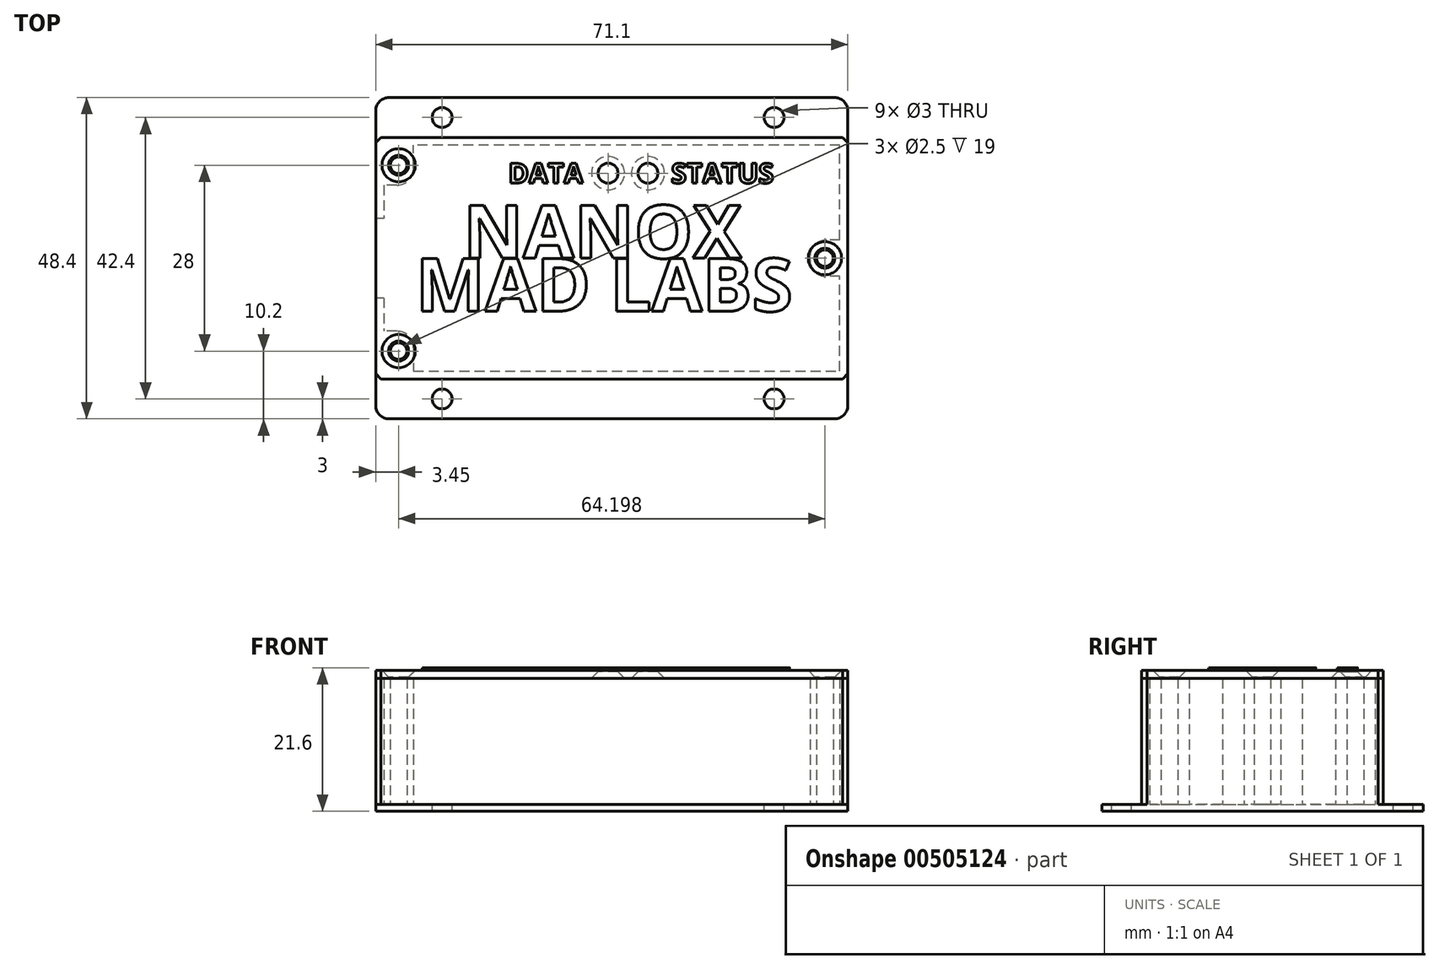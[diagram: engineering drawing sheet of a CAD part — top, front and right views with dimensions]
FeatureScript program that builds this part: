
annotation { "Feature Type Name" : "Feature", "Feature Type Description" : "" }
export const myFeature = defineFeature(function(context is Context, id is Id, definition is map)
    precondition{}
    {
        {
            var Q0;
            Q0=qCreatedBy(makeId("Top.planeOp"),FACE);
            var sketch = newSketch(context, id + "F0", { "sketchPlane" : qUnion([Q0])});
            skLineSegment(sketch, "E0", {"start": v(0, 6) * mm, "end": v(71.1, 6) * mm});
            skLineSegment(sketch, "E1", {"start": v(71.1, 6) * mm, "end": v(71.1, 42.4) * mm});
            skLineSegment(sketch, "E2", {"start": v(71.1, 42.4) * mm, "end": v(0, 42.4) * mm});
            skLineSegment(sketch, "E3", {"start": v(1.2, 18.2) * mm, "end": v(0, 18.2) * mm});
            skLineSegment(sketch, "E4", {"start": v(0, 18.2) * mm, "end": v(0, 6) * mm});
            skLineSegment(sketch, "E5", {"start": v(1.2, 30.2) * mm, "end": v(0, 30.2) * mm});
            skLineSegment(sketch, "E6", {"start": v(0, 30.2) * mm, "end": v(0, 42.4) * mm});
            skLineSegment(sketch, "E7", {"start": v(0, 6) * mm, "end": v(0, 0) * mm});
            skLineSegment(sketch, "E8", {"start": v(0, 0) * mm, "end": v(71.1, 0) * mm});
            skLineSegment(sketch, "E9", {"start": v(71.1, 48.4) * mm, "end": v(0, 48.4) * mm});
            skLineSegment(sketch, "E10", {"start": v(0, 42.4) * mm, "end": v(0, 48.4) * mm});
            skLineSegment(sketch, "E11", {"start": v(71.1, 0) * mm, "end": v(71.1, 6) * mm});
            skLineSegment(sketch, "E12", {"start": v(71.1, 42.4) * mm, "end": v(71.1, 48.4) * mm});
            skCircle(sketch, "E13", {"center": v(10, 3) * mm, "radius": 1.5 * mm});
            skCircle(sketch, "E14", {"center": v(60, 3) * mm, "radius": 1.5 * mm});
            skCircle(sketch, "E15", {"center": v(10, 45.4) * mm, "radius": 1.5 * mm});
            skLineSegment(sketch, "E16", {"start": v(60, 45.4) * mm, "end": v(60, 3) * mm, "construction": true});
            skLineSegment(sketch, "E17", {"start": v(10, 45.4) * mm, "end": v(10, 3) * mm, "construction": true});
            skCircle(sketch, "E18", {"center": v(60, 45.4) * mm, "radius": 1.5 * mm});
            skLineSegment(sketch, "E19", {"start": v(10, 45.4) * mm, "end": v(60, 45.4) * mm, "construction": true});
            skLineSegment(sketch, "E20", {"start": v(60, 3) * mm, "end": v(10, 3) * mm, "construction": true});
            skLineSegment(sketch, "E21", {"start": v(0, 18.2) * mm, "end": v(0, 30.2) * mm});
            skLineSegment(sketch, "E22", {"start": v(3.45, 10.2) * mm, "end": v(3.45, 38.2) * mm, "construction": true});
            skCircle(sketch, "E23", {"center": v(3.45, 38.2) * mm, "radius": 1.25 * mm});
            skCircle(sketch, "E24", {"center": v(3.45, 10.2) * mm, "radius": 1.25 * mm});
            skLineSegment(sketch, "E25.bottom", {"start": v(5.7, 13.2) * mm, "end": v(1.2, 13.2) * mm});
            skLineSegment(sketch, "E25.left", {"start": v(5.7, 13.2) * mm, "end": v(5.7, 7.2) * mm});
            skLineSegment(sketch, "E26.bottom", {"start": v(5.7, 35.2) * mm, "end": v(1.2, 35.2) * mm});
            skLineSegment(sketch, "E26.left", {"start": v(5.7, 35.2) * mm, "end": v(5.7, 41.2) * mm});
            skLineSegment(sketch, "E27.bottom", {"start": v(69.9, 21.45) * mm, "end": v(65.4, 21.45) * mm});
            skLineSegment(sketch, "E27.top", {"start": v(69.9, 26.95) * mm, "end": v(65.4, 26.95) * mm});
            skLineSegment(sketch, "E27.right", {"start": v(65.4, 21.45) * mm, "end": v(65.4, 26.95) * mm});
            skCircle(sketch, "E28", {"center": v(67.65, 24.2) * mm, "radius": 1.25 * mm});
            skLineSegment(sketch, "E29", {"start": v(5.7, 7.2) * mm, "end": v(69.9, 7.2) * mm});
            skLineSegment(sketch, "E30", {"start": v(1.2, 35.2) * mm, "end": v(1.2, 30.2) * mm});
            skLineSegment(sketch, "E31", {"start": v(1.2, 18.2) * mm, "end": v(1.2, 13.2) * mm});
            skLineSegment(sketch, "E32", {"start": v(69.9, 41.2) * mm, "end": v(5.7, 41.2) * mm});
            skLineSegment(sketch, "E33", {"start": v(69.9, 7.2) * mm, "end": v(69.9, 21.45) * mm});
            skLineSegment(sketch, "E34", {"start": v(69.9, 26.95) * mm, "end": v(69.9, 41.2) * mm});
            skSolve(sketch);
        }
        {
            var Q0;
            Q0=makeQuery(id+"F0.imprint","IMPRINT",FACE,{"disambiguationData":[TD([[makeQuery(id+"F0.imprint","IMPRINT",EDGE,{"derivedFrom":sQuery(id+"F0.wireOp",EDGE,"9c3Mvh7g-mxJt-K1xE-6H6P-Ljy5htNZZuxI")}),1.0]])]});
            var Q1;
            Q1=makeQuery(id+"F0.imprint","IMPRINT",FACE,{"disambiguationData":[TD([[makeQuery(id+"F0.imprint","IMPRINT",EDGE,{"derivedFrom":sQuery(id+"F0.wireOp",EDGE,"E0")}),1.0]])]});
            extrude(context, id + "F1", {"entities" : qUnion([Q0, Q1]), "depth" : 19 * mm});
        }
        {
            var Q0;
            Q0 = qSketchRegion(id + "F0", true);
            var Q1;
            Q1=makeQuery(id+"F0.imprint","IMPRINT",FACE,{"disambiguationData":[TD([[makeQuery(id+"F0.imprint","IMPRINT",EDGE,{"derivedFrom":sQuery(id+"F0.wireOp",EDGE,"E27.bottom")}),-1.0]])]});
            var Q2;
            Q2=makeQuery(id+"F0.imprint","IMPRINT",FACE,{"disambiguationData":[TD([[makeQuery(id+"F0.imprint","IMPRINT",EDGE,{"derivedFrom":sQuery(id+"F0.wireOp",EDGE,"E24")}),-1.0]])]});
            var Q3;
            Q3=makeQuery(id+"F0.imprint","IMPRINT",FACE,{"disambiguationData":[TD([[makeQuery(id+"F0.imprint","IMPRINT",EDGE,{"derivedFrom":sQuery(id+"F0.wireOp",EDGE,"E23")}),-1.0]])]});
            var Q4;
            Q4=makeQuery(id+"F0.imprint","IMPRINT",FACE,{"disambiguationData":[TD([[makeQuery(id+"F0.imprint","IMPRINT",EDGE,{"derivedFrom":sQuery(id+"F0.wireOp",EDGE,"E24")}),1.0]])]});
            var Q5;
            Q5=makeQuery(id+"F0.imprint","IMPRINT",FACE,{"disambiguationData":[TD([[makeQuery(id+"F0.imprint","IMPRINT",EDGE,{"derivedFrom":sQuery(id+"F0.wireOp",EDGE,"E28")}),1.0]])]});
            var Q6;
            Q6=makeQuery(id+"F0.imprint","IMPRINT",FACE,{"disambiguationData":[TD([[makeQuery(id+"F0.imprint","IMPRINT",EDGE,{"derivedFrom":sQuery(id+"F0.wireOp",EDGE,"E23")}),1.0]])]});
            extrude(context, id + "F2", {"entities" : qUnion([Q0, Q1, Q2, Q3, Q4, Q5, Q6]), "operationType" : NewBodyOperationType.ADD, "depth" : -1 * mm});
        }
        {
            var Q0;
            Q0=makeQuery(id+"F2.opExtrude","SWEPT_EDGE",EDGE,{"disambiguationData":[OSD([sQuery(id+"F0.wireOp",EDGE,"E7"),sQuery(id+"F0.wireOp",EDGE,"E8")])]});
            var Q1;
            Q1=makeQuery(id+"F2.opExtrude","SWEPT_EDGE",EDGE,{"disambiguationData":[OSD([sQuery(id+"F0.wireOp",EDGE,"E8"),sQuery(id+"F0.wireOp",EDGE,"E11")])]});
            var Q2;
            Q2=makeQuery(id+"F2.opExtrude","SWEPT_EDGE",EDGE,{"disambiguationData":[OSD([sQuery(id+"F0.wireOp",EDGE,"E9"),sQuery(id+"F0.wireOp",EDGE,"E12")])]});
            var Q3;
            Q3=makeQuery(id+"F2.opExtrude","SWEPT_EDGE",EDGE,{"disambiguationData":[OSD([sQuery(id+"F0.wireOp",EDGE,"E9"),sQuery(id+"F0.wireOp",EDGE,"E10")])]});
            fillet(context, id + "F3", {"entities" : qUnion([Q0, Q1, Q2, Q3]), "radius" : 2 * mm, "tangentPropagation" : true, "allowEdgeOverflow" : false});
        }
        {
            var Q0;
            Q0=makeQuery(id+"F1.opExtrude","SWEPT_EDGE",EDGE,{"disambiguationData":[OSD([sQuery(id+"F0.wireOp",EDGE,"E2"),sQuery(id+"F0.wireOp",EDGE,"E6"),sQuery(id+"F0.wireOp",EDGE,"E10")])]});
            var Q1;
            Q1=makeQuery(id+"F1.opExtrude","SWEPT_EDGE",EDGE,{"disambiguationData":[OSD([sQuery(id+"F0.wireOp",EDGE,"E0"),sQuery(id+"F0.wireOp",EDGE,"E4"),sQuery(id+"F0.wireOp",EDGE,"E7")])]});
            var Q2;
            Q2=makeQuery(id+"F1.opExtrude","SWEPT_EDGE",EDGE,{"disambiguationData":[OSD([sQuery(id+"F0.wireOp",EDGE,"E0"),sQuery(id+"F0.wireOp",EDGE,"E1"),sQuery(id+"F0.wireOp",EDGE,"E11")])]});
            var Q3;
            Q3=makeQuery(id+"F1.opExtrude","SWEPT_EDGE",EDGE,{"disambiguationData":[OSD([sQuery(id+"F0.wireOp",EDGE,"E1"),sQuery(id+"F0.wireOp",EDGE,"E2"),sQuery(id+"F0.wireOp",EDGE,"E12")])]});
            chamfer(context, id + "F4", {"entities" : qUnion([Q0, Q1, Q2, Q3]), "width" : 0.8 * mm, "tangentPropagation" : true});
        }
        {
            var Q0;
            Q0=makeQuery(id+"F1.opExtrude","SWEPT_EDGE",EDGE,{"disambiguationData":[OSD([sQuery(id+"F0.wireOp",EDGE,"E26.bottom"),sQuery(id+"F0.wireOp",EDGE,"E26.left")])]});
            var Q1;
            Q1=makeQuery(id+"F1.opExtrude","SWEPT_EDGE",EDGE,{"disambiguationData":[OSD([sQuery(id+"F0.wireOp",EDGE,"E27.bottom"),sQuery(id+"F0.wireOp",EDGE,"E27.right")])]});
            var Q2;
            Q2=makeQuery(id+"F1.opExtrude","SWEPT_EDGE",EDGE,{"disambiguationData":[OSD([sQuery(id+"F0.wireOp",EDGE,"E27.top"),sQuery(id+"F0.wireOp",EDGE,"E27.right")])]});
            var Q3;
            Q3=makeQuery(id+"F1.opExtrude","SWEPT_EDGE",EDGE,{"disambiguationData":[OSD([sQuery(id+"F0.wireOp",EDGE,"E25.bottom"),sQuery(id+"F0.wireOp",EDGE,"E25.left")])]});
            fillet(context, id + "F5", {"entities" : qUnion([Q0, Q1, Q2, Q3]), "radius" : 2.5 * mm, "tangentPropagation" : true, "allowEdgeOverflow" : false});
        }
        {
            var Q0;
            Q0=makeQuery(id+"F1.opExtrude","CAP_FACE",FACE,{"disambiguationData":[OSD([sQuery(id+"F0.wireOp",EDGE,"E0"),sQuery(id+"F0.wireOp",EDGE,"E1"),sQuery(id+"F0.wireOp",EDGE,"E2"),sQuery(id+"F0.wireOp",EDGE,"E3"),sQuery(id+"F0.wireOp",EDGE,"E4"),sQuery(id+"F0.wireOp",EDGE,"E5"),sQuery(id+"F0.wireOp",EDGE,"E6"),sQuery(id+"F0.wireOp",EDGE,"E23"),sQuery(id+"F0.wireOp",EDGE,"E24"),sQuery(id+"F0.wireOp",EDGE,"E25.bottom"),sQuery(id+"F0.wireOp",EDGE,"E25.left"),sQuery(id+"F0.wireOp",EDGE,"E26.bottom"),sQuery(id+"F0.wireOp",EDGE,"E26.left"),sQuery(id+"F0.wireOp",EDGE,"E27.bottom"),sQuery(id+"F0.wireOp",EDGE,"E27.top"),sQuery(id+"F0.wireOp",EDGE,"E27.right"),sQuery(id+"F0.wireOp",EDGE,"E28"),sQuery(id+"F0.wireOp",EDGE,"E29"),sQuery(id+"F0.wireOp",EDGE,"E30"),sQuery(id+"F0.wireOp",EDGE,"E31"),sQuery(id+"F0.wireOp",EDGE,"E32"),sQuery(id+"F0.wireOp",EDGE,"E33"),sQuery(id+"F0.wireOp",EDGE,"E34")])],"isStart":false});
            var sketch = newSketch(context, id + "F6", { "sketchPlane" : qUnion([Q0])});
            skLineSegment(sketch, "E35", {"start": v(0, 42.4) * mm, "end": v(71.1, 42.4) * mm});
            skLineSegment(sketch, "E36", {"start": v(71.1, 42.4) * mm, "end": v(71.1, 6) * mm});
            skLineSegment(sketch, "E37", {"start": v(71.1, 6) * mm, "end": v(0, 6) * mm});
            skLineSegment(sketch, "E38", {"start": v(0, 6) * mm, "end": v(0, 42.4) * mm});
            skCircle(sketch, "E39", {"center": v(3.45, 38.2) * mm, "radius": 1.5 * mm});
            skCircle(sketch, "E40", {"center": v(3.45, 10.2) * mm, "radius": 1.5 * mm});
            skCircle(sketch, "E41", {"center": v(67.65, 24.2) * mm, "radius": 1.5 * mm});
            skLineSegment(sketch, "E42", {"start": v(3.45, 38.2) * mm, "end": v(3.45, 10.2) * mm, "construction": true});
            skLineSegment(sketch, "E43", {"start": v(73.5, 37) * mm, "end": v(-2.79, 37) * mm, "construction": true});
            skCircle(sketch, "E44", {"center": v(35, 37) * mm, "radius": 1.5 * mm});
            skCircle(sketch, "E45", {"center": v(41, 37) * mm, "radius": 1.5 * mm});
            skSolve(sketch);
        }
        {
            var Q0;
            Q0 = qSketchRegion(id + "F6", true);
            extrude(context, id + "F7", {"entities" : qUnion([Q0]), "depth" : 1.2 * mm});
        }
        {
            var Q0;
            Q0=makeQuery(id+"F7.opExtrude","SWEPT_EDGE",EDGE,{"disambiguationData":[OSD([sQuery(id+"F6.wireOp",EDGE,"E37"),sQuery(id+"F6.wireOp",EDGE,"E38")])]});
            var Q1;
            Q1=makeQuery(id+"F7.opExtrude","SWEPT_EDGE",EDGE,{"disambiguationData":[OSD([sQuery(id+"F6.wireOp",EDGE,"E36"),sQuery(id+"F6.wireOp",EDGE,"E37")])]});
            var Q2;
            Q2=makeQuery(id+"F7.opExtrude","SWEPT_EDGE",EDGE,{"disambiguationData":[OSD([sQuery(id+"F6.wireOp",EDGE,"E35"),sQuery(id+"F6.wireOp",EDGE,"E36")])]});
            var Q3;
            Q3=makeQuery(id+"F7.opExtrude","SWEPT_EDGE",EDGE,{"disambiguationData":[OSD([sQuery(id+"F6.wireOp",EDGE,"E35"),sQuery(id+"F6.wireOp",EDGE,"E38")])]});
            chamfer(context, id + "F8", {"entities" : qUnion([Q0, Q1, Q2, Q3]), "width" : 0.8 * mm, "tangentPropagation" : true});
        }
        {
            var Q0;
            Q0=makeQuery(id+"F7.opExtrude","CAP_EDGE",EDGE,{"disambiguationData":[OSD([sQuery(id+"F6.wireOp",EDGE,"E40")])],"isStart":false});
            var Q1;
            Q1=makeQuery(id+"F7.opExtrude","CAP_EDGE",EDGE,{"disambiguationData":[OSD([sQuery(id+"F6.wireOp",EDGE,"E39")])],"isStart":false});
            var Q2;
            Q2=makeQuery(id+"F7.opExtrude","CAP_EDGE",EDGE,{"disambiguationData":[OSD([sQuery(id+"F6.wireOp",EDGE,"E41")])],"isStart":false});
            var Q3;
            Q3=makeQuery(id+"F7.opExtrude","CAP_EDGE",EDGE,{"disambiguationData":[OSD([sQuery(id+"F6.wireOp",EDGE,"E45")])],"isStart":true});
            var Q4;
            Q4=makeQuery(id+"F7.opExtrude","CAP_EDGE",EDGE,{"disambiguationData":[OSD([sQuery(id+"F6.wireOp",EDGE,"E44")])],"isStart":true});
            chamfer(context, id + "F9", {"entities" : qUnion([Q0, Q1, Q2, Q3, Q4]), "width" : 1 * mm, "tangentPropagation" : true});
        }
        {
            var Q0;
            Q0=makeQuery(id+"F7.opExtrude","CAP_FACE",FACE,{"disambiguationData":[OSD([sQuery(id+"F6.wireOp",EDGE,"E35"),sQuery(id+"F6.wireOp",EDGE,"E36"),sQuery(id+"F6.wireOp",EDGE,"E37"),sQuery(id+"F6.wireOp",EDGE,"E38"),sQuery(id+"F6.wireOp",EDGE,"E39"),sQuery(id+"F6.wireOp",EDGE,"E40"),sQuery(id+"F6.wireOp",EDGE,"E41"),sQuery(id+"F6.wireOp",EDGE,"E44"),sQuery(id+"F6.wireOp",EDGE,"E45")])],"isStart":false});
            var sketch = newSketch(context, id + "F10", { "sketchPlane" : qUnion([Q0])});
            skLineSegment(sketch, "E46", {"start": v(70.15, 24.2) * mm, "end": v(0, 24.2) * mm, "construction": true});
            skPoint(sketch, "E46.startSnap0", {"position": v(0, 24.2) * mm});
            skText(sketch, "E47", { "text": "NANOX", "fontName": "OpenSans-Bold.ttf"});
            skText(sketch, "E48", { "text": "MAD LABS", "fontName": "OpenSans-Bold.ttf"});
            skLineSegment(sketch, "E49", {"start": v(0, 35.5) * mm, "end": v(71.1, 35.5) * mm, "construction": true});
            skText(sketch, "E50", { "text": "DATA", "fontName": "OpenSans-Bold.ttf"});
            skText(sketch, "E51", { "text": "STATUS", "fontName": "OpenSans-Bold.ttf"});
            const initialGuessF10  = {"E47": [0.01318, 0.0242, 1, 0, 0.008], "E48": [0.006, 0.0162, 1, 0, 0.008], "E50": [0.01998, 0.0355, 1, 0, 0.003], "E51": [0.0445, 0.0355, 1, 0, 0.003]};
            skSetInitialGuess(sketch, initialGuessF10);
            skSolve(sketch);
        }
        {
            var Q0;
            Q0 = qSketchRegion(id + "F10", true);
            extrude(context, id + "F11", {"entities" : qUnion([Q0]), "operationType" : NewBodyOperationType.ADD, "depth" : 0.4 * mm});
        }
    });
